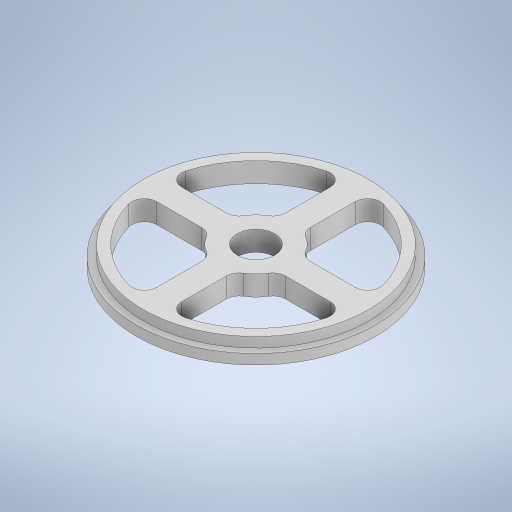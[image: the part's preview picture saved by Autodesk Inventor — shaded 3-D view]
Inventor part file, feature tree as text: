
AUTODESK INVENTOR PART (.ipt)
format: ipt  version: 2024 (Build 280153000, 153)  size: 449,536 bytes
history: native  units: mm
features: extrude x7, sketch x5, projected_geometry x4, fillet x1
ambient origin geometry x8: Origin, YZ Plane, XZ Plane, XY Plane, X Axis, Y Axis, Z Axis, Center Point
bodies: Solide1 (feature_tree)
feature tree (17):
  sketch  "Esquisse1"
  extrude  "Extrusion1"  Depth=15.0mm
  extrude  "Extrusion2"  Depth=90.31mm
  extrude  "Extrusion3"  Depth=95.72mm
  fillet  "Congé1"  Radius=4.0mm
  extrude  "Extrusion4"  Depth=8.0mm TaperAngle=0.0deg
  extrude  "Extrusion5"  Depth=7.0mm
  sketch  "Esquisse5"
  extrude  "Extrusion6"  Depth=4.0mm
  extrude  "Extrusion7"  Depth=5.0mm
  sketch  "Esquisse2"
  projected_geometry  "Boucle projetée1"
  sketch  "Esquisse3"
  projected_geometry  "Boucle projetée2"
  sketch  "Esquisse4"
  projected_geometry  "Boucle projetée3"
  projected_geometry  "Boucle projetée4"
